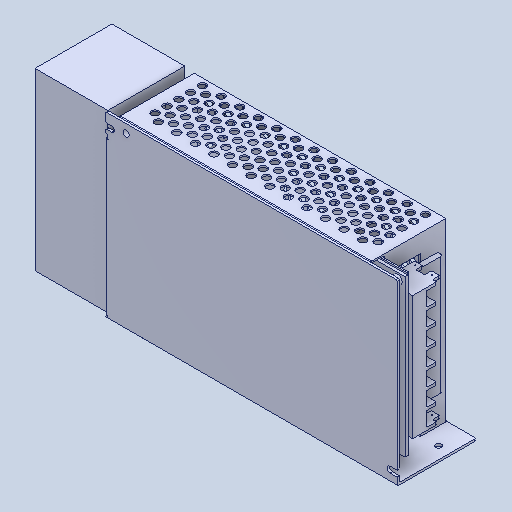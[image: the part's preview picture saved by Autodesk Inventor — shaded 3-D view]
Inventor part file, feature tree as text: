
AUTODESK INVENTOR PART (.ipt)
format: ipt  version: 2023 (Build 270158000, 158)  size: 902,656 bytes
history: native  units: mm
features: other x8, fillet x2, extrude x1, sketch x1
ambient origin geometry x8: Origin, YZ Plane, XZ Plane, XY Plane, X Axis, Y Axis, Z Axis, Center Point
bodies: Solid1 (feature_tree), Solid2 (feature_tree), Solid3 (feature_tree), Solid4 (feature_tree), Solid5 (feature_tree), Solid6 (feature_tree), Solid7 (feature_tree), Solid8 (feature_tree), Solid9 (feature_tree), Solid10 (feature_tree)
feature tree (12):
  extrude  "Extrusion1"  [1 undecoded]
  sketch  "Sketch1"  dims[d0=40.0mm d1=0.0mm]
  other  "Boss-Extrude7"
  other  "LPattern2[1]"
  other  "LPattern2[2]"
  other  "LPattern2[3]"
  other  "LPattern2[4]"
  other  "LPattern2[5]"
  other  "LPattern2[6]"
  other  "Cut-Extrude14[2]"
  fillet  "Fillet9"  [1 undecoded]
  fillet  "Fillet10"  [1 undecoded]
note: 3 required parameter values undecoded (feature->parameter linkage not recoverable at this tier; creation-order binding heuristic only, values carry confidence <= 0.55)
